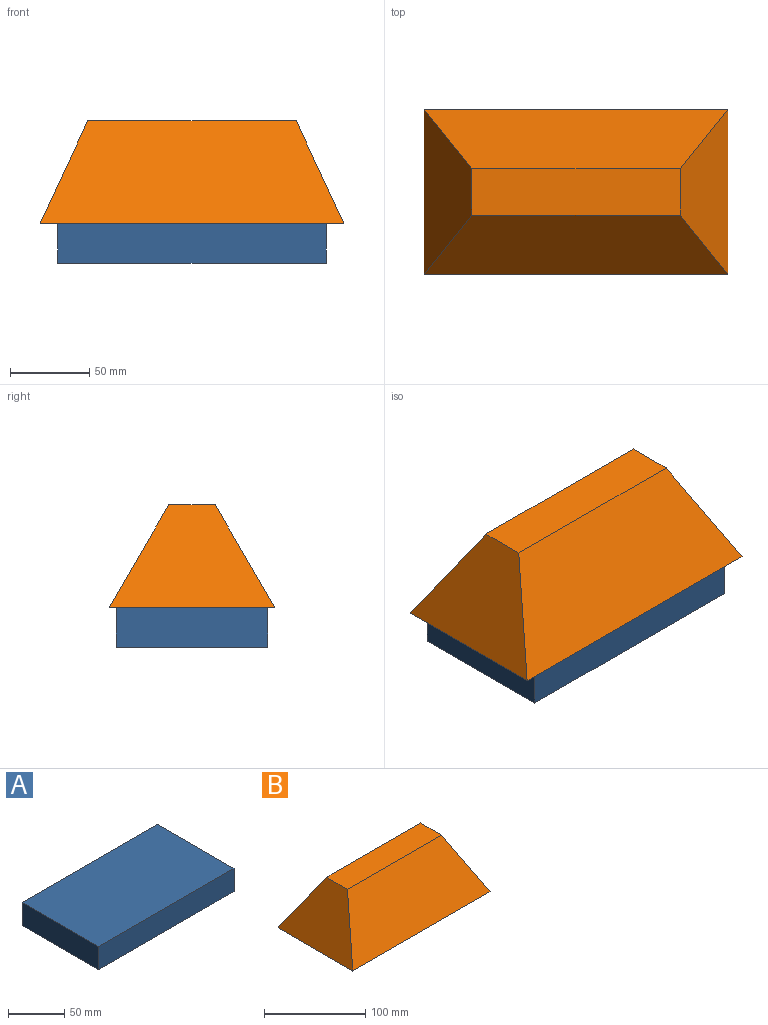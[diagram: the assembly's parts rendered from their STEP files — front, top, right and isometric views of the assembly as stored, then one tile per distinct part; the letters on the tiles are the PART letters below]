
ASSEMBLY  parts=2 mates=1
PART A: 6 faces, bbox 169.7x96x25 mm
  f0: plane 169.72x25mm, normal (0,1,0), area 4242.9mm2, adj f1,f3,f4,f5
  f1: plane 95.96x25mm, normal (-1,0,0), area 2399.1mm2, adj f0,f2,f4,f5
  f2: plane 169.72x25mm, normal (0,-1,0), area 4242.9mm2, adj f1,f3,f4,f5
  f3: plane 95.96x25mm, normal (1,0,0), area 2399.1mm2, adj f0,f2,f4,f5
  f4: plane 169.72x95.96mm, normal (0,0,1), area 16286.8mm2, adj f0,f1,f2,f3
  f5: plane 169.72x95.96mm, normal (0,0,-1), area 16286.8mm2, adj f0,f1,f2,f3
PART B: 6 faces, bbox 192.1x104.7x65 mm
  f0: plane 192.1x104.71mm, normal (0,0,-1), area 20115.2mm2, adj f2,f3,f4,f5
  f1: plane 131.76x29.38mm, normal (0,0,1), area 3870.9mm2, adj f2,f3,f4,f5
  f2: plane 104.71x65mm, normal (0.91,0,0.42), area 4804.6mm2, adj f0,f1,f3,f5
  f3: plane 192.1x65mm, normal (0,0.87,0.5), area 12164.8mm2, adj f0,f1,f2,f4
  f4: plane 104.71x65mm, normal (-0.91,0,0.42), area 4804.6mm2, adj f0,f1,f3,f5
  f5: plane 192.1x65mm, normal (0,-0.87,0.5), area 12164.8mm2, adj f0,f1,f2,f4
PLACE A t=(10,1.44,23)mm
PLACE B t=(0,0,48)mm
MATE fastened A.f4 <-> B.f0  axis (0,0,1) through (0,0,48)mm
